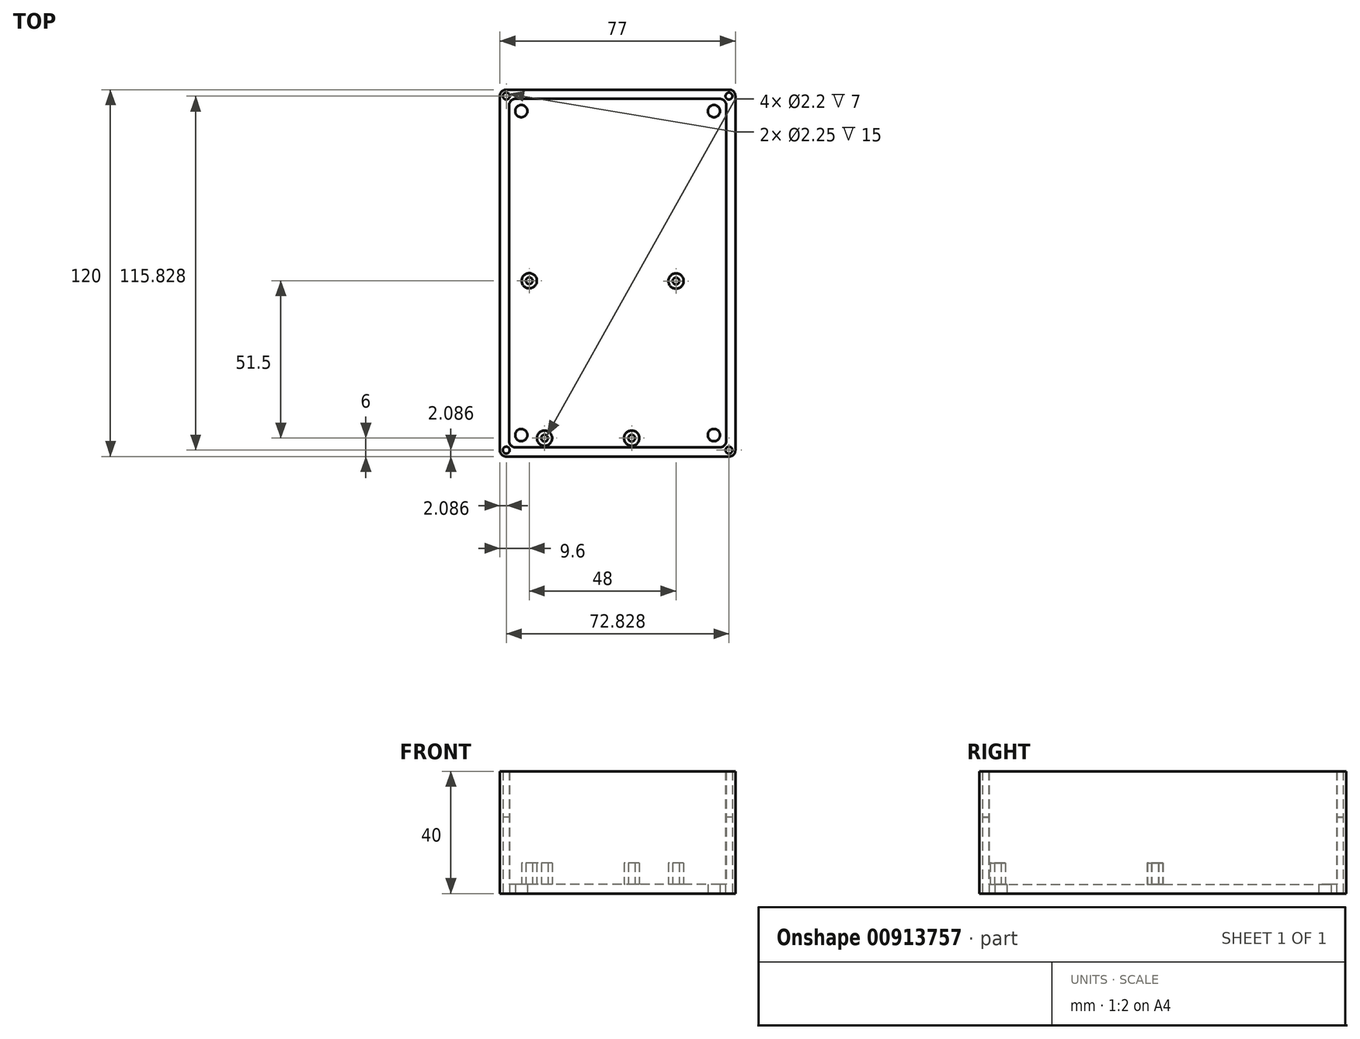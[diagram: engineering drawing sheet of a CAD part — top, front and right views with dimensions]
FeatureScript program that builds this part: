
annotation { "Feature Type Name" : "Feature", "Feature Type Description" : "" }
export const myFeature = defineFeature(function(context is Context, id is Id, definition is map)
    precondition{}
    {
        {
            var Q0;
            Q0=qCreatedBy(makeId("Top.planeOp"),FACE);
            var sketch = newSketch(context, id + "F0", { "sketchPlane" : qUnion([Q0])});
            skLineSegment(sketch, "E0.bottom", {"start": v(-75, 120) * mm, "end": v(-2, 120) * mm});
            skLineSegment(sketch, "E0.top", {"start": v(-75, 0) * mm, "end": v(-2, 0) * mm});
            skLineSegment(sketch, "E0.left", {"start": v(-77, 118) * mm, "end": v(-77, 2) * mm});
            skLineSegment(sketch, "E0.right", {"start": v(0, 118) * mm, "end": v(0, 2) * mm});
            skLineSegment(sketch, "E1", {"start": v(-38.5, 120) * mm, "end": v(-38.5, 0) * mm, "construction": true});
            skLineSegment(sketch, "E2", {"start": v(-77, 60) * mm, "end": v(0, 60) * mm, "construction": true});
            skCircle(sketch, "E3", {"center": v(-70, 113) * mm, "radius": 2 * mm});
            skCircle(sketch, "E4.MirrorC", {"center": v(-7, 113) * mm, "radius": 2 * mm});
            skCircle(sketch, "E5.MirrorC", {"center": v(-70, 7) * mm, "radius": 2 * mm});
            skCircle(sketch, "E6.MirrorC", {"center": v(-7, 7) * mm, "radius": 2 * mm});
            skLineSegment(sketch, "E7", {"start": v(-38.5, 117) * mm, "end": v(-5, 117) * mm});
            skLineSegment(sketch, "E8", {"start": v(-3, 115) * mm, "end": v(-3, 60) * mm});
            skPoint(sketch, "E9.visualSharp", {"position": v(-3, 117) * mm});
            skArc(sketch, "E9.filletArc", {"start": v(-3, 115) * mm, "mid": v(-3.59, 116.41) * mm, "end": v(-5, 117) * mm});
            skPoint(sketch, "E10.visualSharp", {"position": v(0, 120) * mm});
            skArc(sketch, "E10.filletArc", {"start": v(0, 118) * mm, "mid": v(-0.59, 119.41) * mm, "end": v(-2, 120) * mm});
            skPoint(sketch, "E11.visualSharp", {"position": v(-77, 120) * mm});
            skArc(sketch, "E11.filletArc", {"start": v(-75, 120) * mm, "mid": v(-76.41, 119.41) * mm, "end": v(-77, 118) * mm});
            skPoint(sketch, "E12.visualSharp", {"position": v(-77, 0) * mm});
            skArc(sketch, "E12.filletArc", {"start": v(-77, 2) * mm, "mid": v(-76.41, 0.59) * mm, "end": v(-75, 0) * mm});
            skPoint(sketch, "E13.visualSharp", {"position": v(0, 0) * mm});
            skArc(sketch, "E13.filletArc", {"start": v(-2, 0) * mm, "mid": v(-0.59, 0.59) * mm, "end": v(0, 2) * mm});
            skLineSegment(sketch, "E14.MirrorCS", {"start": v(-38.5, 117) * mm, "end": v(-72, 117) * mm});
            skLineSegment(sketch, "E15.MirrorCS", {"start": v(-74, 115) * mm, "end": v(-74, 60) * mm});
            skArc(sketch, "E16.MirrorCS", {"start": v(-74, 115) * mm, "mid": v(-73.41, 116.41) * mm, "end": v(-72, 117) * mm});
            skLineSegment(sketch, "E17.MirrorCS", {"start": v(-38.5, 3) * mm, "end": v(-72, 3) * mm});
            skLineSegment(sketch, "E18.MirrorCS", {"start": v(-38.5, 3) * mm, "end": v(-5, 3) * mm});
            skArc(sketch, "E19.MirrorCS", {"start": v(-74, 5) * mm, "mid": v(-73.41, 3.59) * mm, "end": v(-72, 3) * mm});
            skLineSegment(sketch, "E20.MirrorCS", {"start": v(-74, 5) * mm, "end": v(-74, 60) * mm});
            skArc(sketch, "E21.MirrorCS", {"start": v(-3, 5) * mm, "mid": v(-3.59, 3.59) * mm, "end": v(-5, 3) * mm});
            skLineSegment(sketch, "E22.MirrorCS", {"start": v(-3, 5) * mm, "end": v(-3, 60) * mm});
            skCircle(sketch, "E23", {"center": v(-19.4, 57.4) * mm, "radius": 2.5 * mm});
            skCircle(sketch, "E24", {"center": v(-19.4, 57.4) * mm, "radius": 1.1 * mm});
            skCircle(sketch, "E25", {"center": v(-67.4, 57.5) * mm, "radius": 2.5 * mm});
            skCircle(sketch, "E26", {"center": v(-67.4, 57.5) * mm, "radius": 1.1 * mm});
            skCircle(sketch, "E27", {"center": v(-62.4, 6) * mm, "radius": 2.5 * mm});
            skCircle(sketch, "E28", {"center": v(-62.4, 6) * mm, "radius": 1.1 * mm});
            skCircle(sketch, "E29", {"center": v(-33.9, 6) * mm, "radius": 2.5 * mm});
            skCircle(sketch, "E30", {"center": v(-33.9, 6) * mm, "radius": 1.1 * mm});
            skLineSegment(sketch, "E31", {"start": v(-74.33, 0) * mm, "end": v(71.39, 0) * mm, "construction": true});
            skLineSegment(sketch, "E32", {"start": v(0, 74.6) * mm, "end": v(0, -72.36) * mm, "construction": true});
            skLineSegment(sketch, "E33", {"start": v(-73.41, 116.41) * mm, "end": v(-76.41, 119.41) * mm, "construction": true});
            skCircle(sketch, "E34", {"center": v(-74.91, 117.91) * mm, "radius": 1.13 * mm});
            skCircle(sketch, "E35.MirrorC", {"center": v(-2.09, 117.91) * mm, "radius": 1.13 * mm});
            skCircle(sketch, "E36.MirrorC", {"center": v(-2.09, 2.09) * mm, "radius": 1.13 * mm});
            skCircle(sketch, "E37.MirrorC", {"center": v(-74.91, 2.09) * mm, "radius": 1.13 * mm});
            skSolve(sketch);
        }
        {
            var Q0;
            Q0=makeQuery(id+"F0.imprint","IMPRINT",FACE,{"disambiguationData":[TD([[makeQuery(id+"F0.imprint","IMPRINT",EDGE,{"derivedFrom":sQuery(id+"F0.wireOp",EDGE,"E0.bottom")}),-1.0]])]});
            extrude(context, id + "F1", {"entities" : qUnion([Q0]), "depth" : 40 * mm, "offsetDistance" : 25 * mm});
        }
        {
            var Q0;
            Q0=makeQuery(id+"F0.imprint","IMPRINT",FACE,{"disambiguationData":[TD([[makeQuery(id+"F0.imprint","IMPRINT",EDGE,{"derivedFrom":sQuery(id+"F0.wireOp",EDGE,"E3")}),-1.0]])]});
            extrude(context, id + "F2", {"entities" : qUnion([Q0]), "operationType" : NewBodyOperationType.ADD, "depth" : 3 * mm, "offsetDistance" : 25 * mm});
        }
        {
            var Q0;
            Q0=makeQuery(id+"F0.imprint","IMPRINT",FACE,{"disambiguationData":[TD([[makeQuery(id+"F0.imprint","IMPRINT",EDGE,{"derivedFrom":sQuery(id+"F0.wireOp",EDGE,"E25")}),1.0]])]});
            var Q1;
            Q1=makeQuery(id+"F0.imprint","IMPRINT",FACE,{"disambiguationData":[TD([[makeQuery(id+"F0.imprint","IMPRINT",EDGE,{"derivedFrom":sQuery(id+"F0.wireOp",EDGE,"E23")}),1.0]])]});
            var Q2;
            Q2=makeQuery(id+"F0.imprint","IMPRINT",FACE,{"disambiguationData":[TD([[makeQuery(id+"F0.imprint","IMPRINT",EDGE,{"derivedFrom":sQuery(id+"F0.wireOp",EDGE,"E29")}),1.0]])]});
            var Q3;
            Q3=makeQuery(id+"F0.imprint","IMPRINT",FACE,{"disambiguationData":[TD([[makeQuery(id+"F0.imprint","IMPRINT",EDGE,{"derivedFrom":sQuery(id+"F0.wireOp",EDGE,"E27")}),1.0]])]});
            extrude(context, id + "F3", {"entities" : qUnion([Q0, Q1, Q2, Q3]), "operationType" : NewBodyOperationType.ADD, "depth" : 10 * mm, "offsetDistance" : 25 * mm});
        }
        {
            var Q0;
            Q0=makeQuery(id+"F0.imprint","IMPRINT",FACE,{"disambiguationData":[TD([[makeQuery(id+"F0.imprint","IMPRINT",EDGE,{"derivedFrom":sQuery(id+"F0.wireOp",EDGE,"E26")}),1.0]])]});
            var Q1;
            Q1=makeQuery(id+"F0.imprint","IMPRINT",FACE,{"disambiguationData":[TD([[makeQuery(id+"F0.imprint","IMPRINT",EDGE,{"derivedFrom":sQuery(id+"F0.wireOp",EDGE,"E24")}),1.0]])]});
            var Q2;
            Q2=makeQuery(id+"F0.imprint","IMPRINT",FACE,{"disambiguationData":[TD([[makeQuery(id+"F0.imprint","IMPRINT",EDGE,{"derivedFrom":sQuery(id+"F0.wireOp",EDGE,"E30")}),1.0]])]});
            var Q3;
            Q3=makeQuery(id+"F0.imprint","IMPRINT",FACE,{"disambiguationData":[TD([[makeQuery(id+"F0.imprint","IMPRINT",EDGE,{"derivedFrom":sQuery(id+"F0.wireOp",EDGE,"E28")}),1.0]])]});
            extrude(context, id + "F4", {"entities" : qUnion([Q0, Q1, Q2, Q3]), "operationType" : NewBodyOperationType.ADD, "depth" : 3 * mm, "offsetDistance" : 25 * mm});
        }
        {
            var Q0;
            Q0=qCreatedBy(makeId("Front.planeOp"),FACE);
            var sketch = newSketch(context, id + "F5", { "sketchPlane" : qUnion([Q0])});
            skCircle(sketch, "E38", {"center": v(-20.12, 20) * mm, "radius": 5 * mm});
            skSolve(sketch);
        }
        {
            var Q0;
            Q0=makeQuery(id+"F5.imprint","IMPRINT",FACE,{"disambiguationData":[TD([[makeQuery(id+"F5.imprint","IMPRINT",EDGE,{"derivedFrom":sQuery(id+"F5.wireOp",EDGE,"E38")}),1.0]])]});
            extrude(context, id + "F6", {"entities" : qUnion([Q0]), "operationType" : NewBodyOperationType.REMOVE, "oppositeDirection" : true, "depth" : 4 * mm, "offsetDistance" : 25 * mm});
        }
        {
            var Q0;
            Q0=makeQuery(id+"F0.imprint","IMPRINT",FACE,{"disambiguationData":[TD([[makeQuery(id+"F0.imprint","IMPRINT",EDGE,{"derivedFrom":sQuery(id+"F0.wireOp",EDGE,"E34")}),1.0]])]});
            var Q1;
            Q1=makeQuery(id+"F0.imprint","IMPRINT",FACE,{"disambiguationData":[TD([[makeQuery(id+"F0.imprint","IMPRINT",EDGE,{"derivedFrom":sQuery(id+"F0.wireOp",EDGE,"E35.MirrorC")}),-1.0]])]});
            var Q2;
            Q2=makeQuery(id+"F0.imprint","IMPRINT",FACE,{"disambiguationData":[TD([[makeQuery(id+"F0.imprint","IMPRINT",EDGE,{"derivedFrom":sQuery(id+"F0.wireOp",EDGE,"E36.MirrorC")}),1.0]])]});
            var Q3;
            Q3=makeQuery(id+"F0.imprint","IMPRINT",FACE,{"disambiguationData":[TD([[makeQuery(id+"F0.imprint","IMPRINT",EDGE,{"derivedFrom":sQuery(id+"F0.wireOp",EDGE,"E37.MirrorC")}),-1.0]])]});
            extrude(context, id + "F7", {"entities" : qUnion([Q0, Q1, Q2, Q3]), "operationType" : NewBodyOperationType.ADD, "depth" : 25 * mm, "offsetDistance" : 25 * mm});
        }
    });
